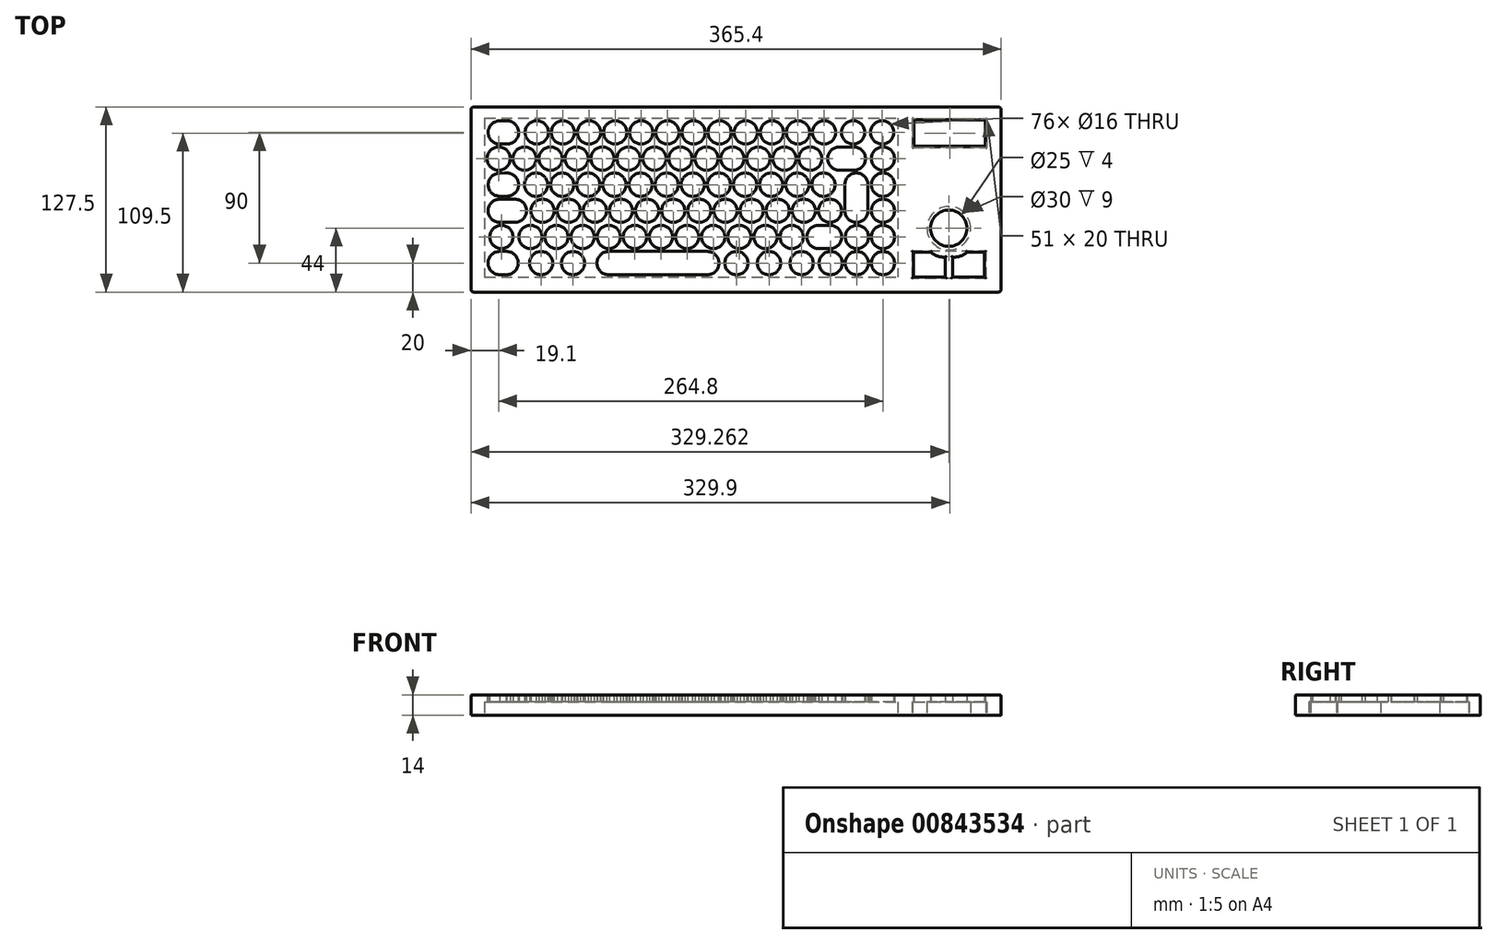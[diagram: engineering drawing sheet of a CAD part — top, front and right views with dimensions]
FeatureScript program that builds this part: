
annotation { "Feature Type Name" : "Feature", "Feature Type Description" : "" }
export const myFeature = defineFeature(function(context is Context, id is Id, definition is map)
    precondition{}
    {
        {
            var Q0;
            Q0=qCreatedBy(makeId("Top.planeOp"),FACE);
            var sketch = newSketch(context, id + "F0", { "sketchPlane" : qUnion([Q0])});
            skCircle(sketch, "E0", {"center": v(41.9, -15.35) * mm, "radius": 8 * mm});
            skLineSegment(sketch, "E1.direction1", {"start": v(41.9, -15.35) * mm, "end": v(59.9, -15.35) * mm, "construction": true});
            skCircle(sketch, "E2", {"center": v(279.9, -15.35) * mm, "radius": 8 * mm});
            skLineSegment(sketch, "E3.left", {"start": v(31.5, -15.34) * mm, "end": v(31.5, -15.34) * mm});
            skLineSegment(sketch, "E3.right", {"start": v(8.4, -15.35) * mm, "end": v(8.4, -15.35) * mm});
            skPoint(sketch, "E3.middle", {"position": v(19.95, -15.35) * mm});
            skPoint(sketch, "E4.visualSharp", {"position": v(8.4, -8.85) * mm});
            skPoint(sketch, "E5.visualSharp", {"position": v(8.4, -21.85) * mm});
            skPoint(sketch, "E6.visualSharp", {"position": v(31.5, -21.84) * mm});
            skPoint(sketch, "E7.visualSharp", {"position": v(31.5, -8.84) * mm});
            skCircle(sketch, "E8", {"center": v(280.4, -33.35) * mm, "radius": 8 * mm});
            skLineSegment(sketch, "E9.left", {"start": v(268.38, -33.35) * mm, "end": v(268.38, -33.35) * mm});
            skLineSegment(sketch, "E9.right", {"start": v(242.38, -33.35) * mm, "end": v(242.38, -33.35) * mm});
            skPoint(sketch, "E9.middle", {"position": v(255.38, -33.35) * mm});
            skPoint(sketch, "E10.visualSharp", {"position": v(242.38, -26.85) * mm});
            skPoint(sketch, "E11.visualSharp", {"position": v(242.38, -39.85) * mm});
            skPoint(sketch, "E12.visualSharp", {"position": v(268.38, -39.85) * mm});
            skPoint(sketch, "E13.visualSharp", {"position": v(268.38, -26.85) * mm});
            skCircle(sketch, "E14", {"center": v(239.4, -51.35) * mm, "radius": 8 * mm});
            skCircle(sketch, "E15", {"center": v(280.4, -51.35) * mm, "radius": 8 * mm});
            skCircle(sketch, "E16.1.0.0", {"center": v(221.4, -51.35) * mm, "radius": 8 * mm});
            skCircle(sketch, "E16.2.0.0", {"center": v(203.4, -51.35) * mm, "radius": 8 * mm});
            skCircle(sketch, "E16.3.0.0", {"center": v(185.4, -51.35) * mm, "radius": 8 * mm});
            skCircle(sketch, "E16.4.0.0", {"center": v(167.4, -51.35) * mm, "radius": 8 * mm});
            skCircle(sketch, "E16.5.0.0", {"center": v(149.4, -51.35) * mm, "radius": 8 * mm});
            skCircle(sketch, "E16.6.0.0", {"center": v(131.4, -51.35) * mm, "radius": 8 * mm});
            skCircle(sketch, "E16.7.0.0", {"center": v(113.4, -51.35) * mm, "radius": 8 * mm});
            skCircle(sketch, "E16.8.0.0", {"center": v(95.4, -51.35) * mm, "radius": 8 * mm});
            skCircle(sketch, "E16.9.0.0", {"center": v(77.4, -51.35) * mm, "radius": 8 * mm});
            skCircle(sketch, "E16.10.0.0", {"center": v(59.4, -51.35) * mm, "radius": 8 * mm});
            skCircle(sketch, "E16.11.0.0", {"center": v(41.4, -51.35) * mm, "radius": 8 * mm});
            skLineSegment(sketch, "E16.direction1", {"start": v(239.4, -51.35) * mm, "end": v(221.4, -51.35) * mm, "construction": true});
            skPoint(sketch, "E17.middle", {"position": v(19.12, -51.3) * mm});
            skCircle(sketch, "E18", {"center": v(280.4, -69.35) * mm, "radius": 8 * mm});
            skCircle(sketch, "E19", {"center": v(217.5, -87.35) * mm, "radius": 8 * mm});
            skCircle(sketch, "E20", {"center": v(262.5, -87.35) * mm, "radius": 8 * mm});
            skCircle(sketch, "E21", {"center": v(280.4, -87.35) * mm, "radius": 8 * mm});
            skLineSegment(sketch, "E22.direction1", {"start": v(217.5, -87.35) * mm, "end": v(199.5, -87.35) * mm, "construction": true});
            skPoint(sketch, "E23.middle", {"position": v(240, -87.35) * mm});
            skCircle(sketch, "E24.0.1.0", {"center": v(199.5, -87.35) * mm, "radius": 8 * mm});
            skCircle(sketch, "E24.0.2.0", {"center": v(181.5, -87.35) * mm, "radius": 8 * mm});
            skCircle(sketch, "E24.0.3.0", {"center": v(163.5, -87.35) * mm, "radius": 8 * mm});
            skCircle(sketch, "E24.0.4.0", {"center": v(145.5, -87.35) * mm, "radius": 8 * mm});
            skCircle(sketch, "E24.0.5.0", {"center": v(127.5, -87.35) * mm, "radius": 8 * mm});
            skCircle(sketch, "E24.0.6.0", {"center": v(109.5, -87.35) * mm, "radius": 8 * mm});
            skCircle(sketch, "E24.0.7.0", {"center": v(91.5, -87.35) * mm, "radius": 8 * mm});
            skCircle(sketch, "E24.0.8.0", {"center": v(73.5, -87.35) * mm, "radius": 8 * mm});
            skCircle(sketch, "E24.0.9.0", {"center": v(55.5, -87.35) * mm, "radius": 8 * mm});
            skCircle(sketch, "E24.0.10.0", {"center": v(37.5, -87.35) * mm, "radius": 8 * mm});
            skCircle(sketch, "E25", {"center": v(44.9, -105.35) * mm, "radius": 8 * mm});
            skCircle(sketch, "E26", {"center": v(66.9, -105.35) * mm, "radius": 8 * mm});
            skCircle(sketch, "E27", {"center": v(179.4, -105.35) * mm, "radius": 8 * mm});
            skCircle(sketch, "E28", {"center": v(201.9, -105.35) * mm, "radius": 8 * mm});
            skCircle(sketch, "E29", {"center": v(224.4, -105.35) * mm, "radius": 8 * mm});
            skCircle(sketch, "E30", {"center": v(244.4, -105.35) * mm, "radius": 8 * mm});
            skCircle(sketch, "E31", {"center": v(262.4, -105.35) * mm, "radius": 8 * mm});
            skCircle(sketch, "E32", {"center": v(280.4, -105.35) * mm, "radius": 8 * mm});
            skLineSegment(sketch, "E33.left", {"start": v(167.4, -105.35) * mm, "end": v(167.4, -105.35) * mm});
            skLineSegment(sketch, "E33.right", {"start": v(83.4, -105.35) * mm, "end": v(83.4, -105.35) * mm});
            skPoint(sketch, "E33.middle", {"position": v(125.4, -105.35) * mm});
            skPoint(sketch, "E34.visualSharp", {"position": v(229.5, -80.85) * mm});
            skPoint(sketch, "E35.visualSharp", {"position": v(250.5, -80.85) * mm});
            skPoint(sketch, "E36.visualSharp", {"position": v(250.5, -93.85) * mm});
            skPoint(sketch, "E37.visualSharp", {"position": v(229.5, -93.85) * mm});
            skPoint(sketch, "E38.visualSharp", {"position": v(167.4, -98.85) * mm});
            skPoint(sketch, "E39.visualSharp", {"position": v(167.4, -111.85) * mm});
            skPoint(sketch, "E40.visualSharp", {"position": v(83.4, -111.85) * mm});
            skPoint(sketch, "E41.visualSharp", {"position": v(83.4, -98.85) * mm});
            skLineSegment(sketch, "E42.bottom", {"start": v(301.9, -6.85) * mm, "end": v(350.9, -6.85) * mm});
            skLineSegment(sketch, "E42.top", {"start": v(301.9, -24.85) * mm, "end": v(350.9, -24.85) * mm});
            skLineSegment(sketch, "E42.left", {"start": v(301.9, -6.85) * mm, "end": v(301.9, -24.85) * mm});
            skLineSegment(sketch, "E42.right", {"start": v(350.9, -6.85) * mm, "end": v(350.9, -24.85) * mm});
            skCircle(sketch, "E43.0.1.0", {"center": v(59.9, -15.35) * mm, "radius": 8 * mm});
            skCircle(sketch, "E43.0.2.0", {"center": v(77.9, -15.35) * mm, "radius": 8 * mm});
            skCircle(sketch, "E43.0.3.0", {"center": v(95.9, -15.35) * mm, "radius": 8 * mm});
            skCircle(sketch, "E43.0.4.0", {"center": v(113.9, -15.35) * mm, "radius": 8 * mm});
            skCircle(sketch, "E43.0.5.0", {"center": v(131.9, -15.35) * mm, "radius": 8 * mm});
            skCircle(sketch, "E43.0.6.0", {"center": v(149.9, -15.35) * mm, "radius": 8 * mm});
            skCircle(sketch, "E43.0.7.0", {"center": v(167.9, -15.35) * mm, "radius": 8 * mm});
            skCircle(sketch, "E43.0.8.0", {"center": v(185.9, -15.35) * mm, "radius": 8 * mm});
            skCircle(sketch, "E43.0.9.0", {"center": v(203.9, -15.35) * mm, "radius": 8 * mm});
            skCircle(sketch, "E43.0.10.0", {"center": v(221.9, -15.35) * mm, "radius": 8 * mm});
            skCircle(sketch, "E43.0.11.0", {"center": v(239.9, -15.35) * mm, "radius": 8 * mm});
            skCircle(sketch, "E44", {"center": v(259.9, -15.35) * mm, "radius": 8 * mm});
            skCircle(sketch, "E45", {"center": v(17.5, -87.35) * mm, "radius": 8 * mm});
            skCircle(sketch, "E46", {"center": v(243.9, -69.35) * mm, "radius": 8 * mm});
            skLineSegment(sketch, "E47.direction1", {"start": v(243.9, -69.35) * mm, "end": v(225.9, -69.35) * mm, "construction": true});
            skLineSegment(sketch, "E48", {"start": v(361.9, 0.15) * mm, "end": v(361.9, -123.35) * mm});
            skLineSegment(sketch, "E49", {"start": v(301.4, -114.85) * mm, "end": v(301.4, -97.85) * mm});
            skLineSegment(sketch, "E50", {"start": v(301.4, -97.85) * mm, "end": v(313.4, -97.85) * mm});
            skLineSegment(sketch, "E51", {"start": v(301.4, -114.85) * mm, "end": v(323.4, -114.85) * mm});
            skLineSegment(sketch, "E52", {"start": v(323.4, -114.85) * mm, "end": v(323.4, -101.35) * mm});
            skLineSegment(sketch, "E53", {"start": v(328.4, -101.35) * mm, "end": v(328.4, -114.85) * mm});
            skLineSegment(sketch, "E54", {"start": v(328.4, -114.85) * mm, "end": v(350.4, -114.85) * mm});
            skLineSegment(sketch, "E55", {"start": v(350.4, -114.85) * mm, "end": v(350.4, -97.85) * mm});
            skLineSegment(sketch, "E56", {"start": v(350.4, -97.85) * mm, "end": v(338.4, -97.85) * mm});
            skArc(sketch, "E57", {"start": v(313.4, -97.85) * mm, "mid": v(318.08, -100.51) * mm, "end": v(323.4, -101.35) * mm});
            skArc(sketch, "E58", {"start": v(328.4, -101.35) * mm, "mid": v(333.72, -100.51) * mm, "end": v(338.4, -97.85) * mm});
            skCircle(sketch, "E59", {"center": v(325.76, -81.35) * mm, "radius": 12.5 * mm});
            skCircle(sketch, "E60", {"center": v(230.4, -33.35) * mm, "radius": 8 * mm});
            skCircle(sketch, "E61.1.0.0", {"center": v(212.5, -33.35) * mm, "radius": 8 * mm});
            skCircle(sketch, "E61.2.0.0", {"center": v(194.6, -33.35) * mm, "radius": 8 * mm});
            skCircle(sketch, "E61.3.0.0", {"center": v(176.7, -33.35) * mm, "radius": 8 * mm});
            skCircle(sketch, "E61.4.0.0", {"center": v(158.8, -33.35) * mm, "radius": 8 * mm});
            skCircle(sketch, "E61.5.0.0", {"center": v(140.9, -33.35) * mm, "radius": 8 * mm});
            skCircle(sketch, "E61.6.0.0", {"center": v(123, -33.35) * mm, "radius": 8 * mm});
            skCircle(sketch, "E61.7.0.0", {"center": v(105.1, -33.35) * mm, "radius": 8 * mm});
            skCircle(sketch, "E61.8.0.0", {"center": v(87.2, -33.35) * mm, "radius": 8 * mm});
            skCircle(sketch, "E61.9.0.0", {"center": v(69.3, -33.35) * mm, "radius": 8 * mm});
            skCircle(sketch, "E61.10.0.0", {"center": v(51.4, -33.35) * mm, "radius": 8 * mm});
            skCircle(sketch, "E61.11.0.0", {"center": v(33.5, -33.35) * mm, "radius": 8 * mm});
            skCircle(sketch, "E61.12.0.0", {"center": v(15.6, -33.35) * mm, "radius": 8 * mm});
            skLineSegment(sketch, "E61.direction1", {"start": v(230.4, -33.35) * mm, "end": v(212.5, -33.35) * mm, "construction": true});
            skCircle(sketch, "E62.0.1.0", {"center": v(225.9, -69.35) * mm, "radius": 8 * mm});
            skCircle(sketch, "E62.0.2.0", {"center": v(207.9, -69.35) * mm, "radius": 8 * mm});
            skCircle(sketch, "E62.0.3.0", {"center": v(189.9, -69.35) * mm, "radius": 8 * mm});
            skCircle(sketch, "E62.0.4.0", {"center": v(171.9, -69.35) * mm, "radius": 8 * mm});
            skCircle(sketch, "E62.0.5.0", {"center": v(153.9, -69.35) * mm, "radius": 8 * mm});
            skCircle(sketch, "E62.0.6.0", {"center": v(135.9, -69.35) * mm, "radius": 8 * mm});
            skCircle(sketch, "E62.0.7.0", {"center": v(117.9, -69.35) * mm, "radius": 8 * mm});
            skCircle(sketch, "E62.0.8.0", {"center": v(99.9, -69.35) * mm, "radius": 8 * mm});
            skCircle(sketch, "E62.0.9.0", {"center": v(81.9, -69.35) * mm, "radius": 8 * mm});
            skCircle(sketch, "E62.0.10.0", {"center": v(63.9, -69.35) * mm, "radius": 8 * mm});
            skCircle(sketch, "E62.0.11.0", {"center": v(45.9, -69.35) * mm, "radius": 8 * mm});
            skPoint(sketch, "E63.endSnap0", {"position": v(280.4, -96.35) * mm});
            skArc(sketch, "E64", {"start": v(91.4, -97.35) * mm, "mid": v(83.4, -105.35) * mm, "end": v(91.4, -113.35) * mm});
            skArc(sketch, "E65", {"start": v(159.4, -113.35) * mm, "mid": v(167.4, -105.35) * mm, "end": v(159.4, -97.35) * mm});
            skLineSegment(sketch, "E66", {"start": v(91.4, -97.35) * mm, "end": v(159.4, -97.35) * mm});
            skLineSegment(sketch, "E67", {"start": v(91.4, -113.35) * mm, "end": v(159.4, -113.35) * mm});
            skArc(sketch, "E68", {"start": v(250.38, -25.35) * mm, "mid": v(242.38, -33.35) * mm, "end": v(250.38, -41.35) * mm});
            skArc(sketch, "E69", {"start": v(260.38, -41.35) * mm, "mid": v(268.38, -33.35) * mm, "end": v(260.38, -25.35) * mm});
            skLineSegment(sketch, "E70", {"start": v(250.38, -25.35) * mm, "end": v(260.38, -25.35) * mm});
            skLineSegment(sketch, "E71", {"start": v(260.38, -41.35) * mm, "end": v(250.38, -41.35) * mm});
            skArc(sketch, "E72", {"start": v(254.15, -69.35) * mm, "mid": v(262.15, -77.35) * mm, "end": v(270.15, -69.35) * mm});
            skArc(sketch, "E73", {"start": v(270.15, -51.35) * mm, "mid": v(262.15, -43.35) * mm, "end": v(254.15, -51.35) * mm});
            skLineSegment(sketch, "E74", {"start": v(254.15, -51.35) * mm, "end": v(254.15, -69.35) * mm});
            skLineSegment(sketch, "E75", {"start": v(270.15, -69.35) * mm, "end": v(270.15, -51.35) * mm});
            skPoint(sketch, "E76.start.orphan", {"position": v(272.4, -69.35) * mm});
            skArc(sketch, "E77", {"start": v(244, -95.35) * mm, "mid": v(252, -87.35) * mm, "end": v(244, -79.35) * mm});
            skLineSegment(sketch, "E78", {"start": v(236, -79.35) * mm, "end": v(244, -79.35) * mm});
            skLineSegment(sketch, "E79", {"start": v(244, -95.35) * mm, "end": v(236, -95.35) * mm});
            skPoint(sketch, "E36.filletArc.start.orphan", {"position": v(244, -93.85) * mm});
            skPoint(sketch, "E80.orphan", {"position": v(244, -80.85) * mm});
            skArc(sketch, "E81.trimOffspring", {"start": v(236, -79.35) * mm, "mid": v(228, -87.35) * mm, "end": v(236, -95.35) * mm});
            skPoint(sketch, "E34.filletArc.start.orphan", {"position": v(236, -80.85) * mm});
            skPoint(sketch, "E37.filletArc.end.orphan", {"position": v(236, -93.85) * mm});
            skArc(sketch, "E82", {"start": v(16.4, -7.37) * mm, "mid": v(8.4, -15.38) * mm, "end": v(16.43, -23.37) * mm});
            skArc(sketch, "E83", {"start": v(21.4, -23.35) * mm, "mid": v(29.4, -15.06) * mm, "end": v(20.83, -7.37) * mm});
            skLineSegment(sketch, "E84", {"start": v(16.43, -23.37) * mm, "end": v(21.4, -23.35) * mm});
            skLineSegment(sketch, "E85", {"start": v(16.4, -7.37) * mm, "end": v(21.4, -7.37) * mm});
            skLineSegment(sketch, "E86", {"start": v(8.33, -51.32) * mm, "end": v(8.4, -51.32) * mm});
            skArc(sketch, "E87", {"start": v(16.33, -43.44) * mm, "mid": v(8.4, -51.37) * mm, "end": v(16.33, -59.3) * mm});
            skArc(sketch, "E88", {"start": v(21.24, -59.3) * mm, "mid": v(29.33, -51.1) * mm, "end": v(20.87, -43.3) * mm});
            skLineSegment(sketch, "E89", {"start": v(16.33, -43.44) * mm, "end": v(21.33, -43.3) * mm});
            skLineSegment(sketch, "E90", {"start": v(21.42, -59.3) * mm, "end": v(16.33, -59.3) * mm});
            skArc(sketch, "E91", {"start": v(16.34, -61.35) * mm, "mid": v(8.34, -69.35) * mm, "end": v(16.34, -77.35) * mm});
            skArc(sketch, "E92", {"start": v(26.84, -77.35) * mm, "mid": v(34.84, -69.35) * mm, "end": v(26.84, -61.35) * mm});
            skLineSegment(sketch, "E93", {"start": v(16.34, -61.35) * mm, "end": v(26.84, -61.35) * mm});
            skLineSegment(sketch, "E94", {"start": v(16.34, -77.35) * mm, "end": v(26.84, -77.35) * mm});
            skArc(sketch, "E95", {"start": v(16.3, -97.33) * mm, "mid": v(8.3, -105.33) * mm, "end": v(16.3, -113.33) * mm});
            skArc(sketch, "E96", {"start": v(21.11, -113.33) * mm, "mid": v(29.11, -105.33) * mm, "end": v(21.11, -97.33) * mm});
            skLineSegment(sketch, "E97", {"start": v(16.3, -97.33) * mm, "end": v(21.11, -97.33) * mm});
            skLineSegment(sketch, "E98", {"start": v(21.11, -113.33) * mm, "end": v(16.3, -113.33) * mm});
            skLineSegment(sketch, "E99.bottom", {"start": v(5.98, -5.47) * mm, "end": v(290.54, -5.47) * mm});
            skLineSegment(sketch, "E99.top", {"start": v(5.98, -114.85) * mm, "end": v(290.54, -114.85) * mm});
            skLineSegment(sketch, "E99.left", {"start": v(5.98, -5.47) * mm, "end": v(5.98, -114.85) * mm});
            skLineSegment(sketch, "E99.right", {"start": v(290.54, -5.47) * mm, "end": v(290.54, -114.85) * mm});
            skLineSegment(sketch, "E100", {"start": v(353.9, -117.35) * mm, "end": v(353.9, -3.85) * mm});
            skLineSegment(sketch, "E101", {"start": v(353.9, -117.35) * mm, "end": v(4.5, -117.35) * mm});
            skLineSegment(sketch, "E102", {"start": v(4.5, -117.35) * mm, "end": v(4.5, -3.85) * mm});
            skLineSegment(sketch, "E103", {"start": v(4.5, -3.85) * mm, "end": v(353.9, -3.85) * mm});
            skCircle(sketch, "E104", {"center": v(325.76, -81.35) * mm, "radius": 15 * mm});
            skLineSegment(sketch, "E105.top", {"start": v(301.4, -115.85) * mm, "end": v(300.4, -115.85) * mm});
            skLineSegment(sketch, "E105.right", {"start": v(300.4, -114.85) * mm, "end": v(300.4, -115.85) * mm});
            skLineSegment(sketch, "E106.top", {"start": v(350.4, -96.85) * mm, "end": v(351.4, -96.85) * mm});
            skLineSegment(sketch, "E106.right", {"start": v(351.4, -97.85) * mm, "end": v(351.4, -96.85) * mm});
            skLineSegment(sketch, "E107.bottom", {"start": v(351.4, -96.85) * mm, "end": v(300.4, -96.85) * mm});
            skLineSegment(sketch, "E107.top", {"start": v(351.4, -115.85) * mm, "end": v(300.4, -115.85) * mm});
            skLineSegment(sketch, "E107.left", {"start": v(351.4, -96.85) * mm, "end": v(351.4, -115.85) * mm});
            skLineSegment(sketch, "E107.right", {"start": v(300.4, -96.85) * mm, "end": v(300.4, -115.85) * mm});
            skLineSegment(sketch, "E108.top", {"start": v(350.9, -25.85) * mm, "end": v(351.9, -25.85) * mm});
            skLineSegment(sketch, "E108.right", {"start": v(351.9, -24.85) * mm, "end": v(351.9, -25.85) * mm});
            skLineSegment(sketch, "E109.top", {"start": v(301.9, -5.85) * mm, "end": v(300.9, -5.85) * mm});
            skLineSegment(sketch, "E109.right", {"start": v(300.9, -6.85) * mm, "end": v(300.9, -5.85) * mm});
            skLineSegment(sketch, "E110.bottom", {"start": v(300.9, -5.85) * mm, "end": v(351.9, -5.85) * mm});
            skLineSegment(sketch, "E110.top", {"start": v(300.9, -25.85) * mm, "end": v(351.9, -25.85) * mm});
            skLineSegment(sketch, "E110.left", {"start": v(300.9, -5.85) * mm, "end": v(300.9, -25.85) * mm});
            skLineSegment(sketch, "E110.right", {"start": v(351.9, -5.85) * mm, "end": v(351.9, -25.85) * mm});
            skLineSegment(sketch, "E111", {"start": v(-1.5, 2.15) * mm, "end": v(359.9, 2.15) * mm});
            skLineSegment(sketch, "E112", {"start": v(-1.5, -125.35) * mm, "end": v(359.9, -125.35) * mm});
            skLineSegment(sketch, "E113", {"start": v(-3.5, -123.35) * mm, "end": v(-3.5, 0.15) * mm});
            skPoint(sketch, "E114.visualSharp", {"position": v(-3.5, 2.15) * mm});
            skArc(sketch, "E114.filletArc", {"start": v(-1.5, 2.15) * mm, "mid": v(-2.91, 1.56) * mm, "end": v(-3.5, 0.15) * mm});
            skPoint(sketch, "E115.visualSharp", {"position": v(-3.5, -125.35) * mm});
            skArc(sketch, "E115.filletArc", {"start": v(-3.5, -123.35) * mm, "mid": v(-2.91, -124.76) * mm, "end": v(-1.5, -125.35) * mm});
            skPoint(sketch, "E116.visualSharp", {"position": v(361.9, -125.35) * mm});
            skArc(sketch, "E116.filletArc", {"start": v(359.9, -125.35) * mm, "mid": v(361.31, -124.76) * mm, "end": v(361.9, -123.35) * mm});
            skPoint(sketch, "E117.visualSharp", {"position": v(361.9, 2.15) * mm});
            skArc(sketch, "E117.filletArc", {"start": v(361.9, 0.15) * mm, "mid": v(361.31, 1.56) * mm, "end": v(359.9, 2.15) * mm});
            skSolve(sketch);
        }
        {
            var Q0;
            Q0=makeQuery(id+"F0.imprint","IMPRINT",FACE,{"disambiguationData":[TD([[makeQuery(id+"F0.imprint","IMPRINT",EDGE,{"derivedFrom":sQuery(id+"F0.wireOp",EDGE,"T8WCm78W-SvFY-fUnR-yLuJ-OhTCZNTdzIay")}),1.0]])]});
            var Q1;
            {var subQ17=sQuery(id+"F0.wireOp",EDGE,"mFOY19iY-rQF4-OdMh-8pD4-EtOYxX6kkBAH");Q1=makeQuery(id+"F0.imprint","IMPRINT",FACE,{"disambiguationData":[TD([[makeQuery(id+"F0.imprint","IMPRINT",EDGE,{"derivedFrom":subQ17}),1.0]])]});}
            var Q2;
            {var subQ4=sQuery(id+"F0.wireOp",EDGE,"O5om7XPq-pfzq-tTJn-29gd-RDgdcxbKojAD");Q2=makeQuery(id+"F0.imprint","IMPRINT",FACE,{"disambiguationData":[TD([[makeQuery(id+"F0.imprint","IMPRINT",EDGE,{"derivedFrom":subQ4}),-1.0]])]});}
            var Q3;
            {var subQ9=sQuery(id+"F0.wireOp",EDGE,"mFOY19iY-rQF4-OdMh-8pD4-EtOYxX6kkBAH");Q3=makeQuery(id+"F0.imprint","IMPRINT",FACE,{"disambiguationData":[TD([[makeQuery(id+"F0.imprint","IMPRINT",EDGE,{"derivedFrom":subQ9}),-1.0]])]});}
            var Q4;
            {var subQ1=sQuery(id+"F0.wireOp",EDGE,"E42.top");Q4=makeQuery(id+"F0.imprint","IMPRINT",FACE,{"disambiguationData":[TD([[makeQuery(id+"F0.imprint","IMPRINT",EDGE,{"derivedFrom":subQ1}),-1.0]])]});}
            var Q5;
            {var subQ0=sQuery(id+"F0.wireOp",EDGE,"IOk0f0ik-m6Pr-axO5-sAgc-cp6PbQEXwRWr");var subQ2=sQuery(id+"F0.wireOp",EDGE,"LzY9nmAe-SVTQ-qMCv-zxcc-P1EQXe39lv1v");var subQ3=makeQuery(id+"F0.imprint","INTERSECT",VERTEX,{"derivedFrom":[subQ2,subQ0]});Q5=makeQuery(id+"F0.imprint","IMPRINT",FACE,{"disambiguationData":[TD([[makeQuery(id+"F0.imprint","IMPRINT",EDGE,{"disambiguationData":[TD([[subQ3,-1.0]])],"derivedFrom":subQ2}),-1.0]])]});}
            var Q6;
            {var subQ7=sQuery(id+"F0.wireOp",EDGE,"IOk0f0ik-m6Pr-axO5-sAgc-cp6PbQEXwRWr");var subQ9=sQuery(id+"F0.wireOp",EDGE,"LzY9nmAe-SVTQ-qMCv-zxcc-P1EQXe39lv1v");var subQ10=makeQuery(id+"F0.imprint","INTERSECT",VERTEX,{"derivedFrom":[subQ9,subQ7]});Q6=makeQuery(id+"F0.imprint","IMPRINT",FACE,{"disambiguationData":[TD([[makeQuery(id+"F0.imprint","IMPRINT",EDGE,{"disambiguationData":[TD([[subQ10,-1.0]])],"derivedFrom":subQ9}),1.0]])]});}
            var Q7;
            {var subQ5=sQuery(id+"F0.wireOp",EDGE,"7YK5K3SY-gkoG-W7Ew-9AiD-mYzw7hBbQorf");Q7=makeQuery(id+"F0.imprint","IMPRINT",FACE,{"disambiguationData":[TD([[makeQuery(id+"F0.imprint","IMPRINT",EDGE,{"derivedFrom":subQ5}),1.0]])]});}
            var Q8;
            {var subQ5=sQuery(id+"F0.wireOp",EDGE,"LzY9nmAe-SVTQ-qMCv-zxcc-P1EQXe39lv1v");var subQ6=makeQuery(id+"F0.imprint","INTERSECT",VERTEX,{"derivedFrom":[subQ5,sQuery(id+"F0.wireOp",EDGE,"PkYXxiHH-amAg-5pAi-YDFA-uypcR8lKY2Dw")]});Q8=makeQuery(id+"F0.imprint","IMPRINT",FACE,{"disambiguationData":[TD([[makeQuery(id+"F0.imprint","IMPRINT",EDGE,{"disambiguationData":[TD([[subQ6,1.0]])],"derivedFrom":subQ5}),1.0]])]});}
            var Q9;
            {var subQ10=sQuery(id+"F0.wireOp",EDGE,"PkYXxiHH-amAg-5pAi-YDFA-uypcR8lKY2Dw");Q9=makeQuery(id+"F0.imprint","IMPRINT",FACE,{"disambiguationData":[TD([[makeQuery(id+"F0.imprint","IMPRINT",EDGE,{"derivedFrom":subQ10}),-1.0]])]});}
            var Q10;
            {var subQ0=sQuery(id+"F0.wireOp",EDGE,"55b4ee8d-2d37-449f-8af8-b3f63763dadd");Q10=makeQuery(id+"F0.imprint","IMPRINT",FACE,{"disambiguationData":[TD([[makeQuery(id+"F0.imprint","IMPRINT",EDGE,{"derivedFrom":subQ0}),1.0]])]});}
            var Q11;
            {var subQ0=sQuery(id+"F0.wireOp",EDGE,"PkYXxiHH-amAg-5pAi-YDFA-uypcR8lKY2Dw");Q11=makeQuery(id+"F0.imprint","IMPRINT",FACE,{"disambiguationData":[TD([[makeQuery(id+"F0.imprint","IMPRINT",EDGE,{"derivedFrom":subQ0}),1.0]])]});}
            var Q12;
            {var subQ0=sQuery(id+"F0.wireOp",EDGE,"2K1XfT52-QnSG-LakS-bHGF-tO5ZBf05Ys4U");Q12=makeQuery(id+"F0.imprint","IMPRINT",FACE,{"disambiguationData":[TD([[makeQuery(id+"F0.imprint","IMPRINT",EDGE,{"derivedFrom":subQ0}),-1.0]])]});}
            var Q13;
            {var subQ7=sQuery(id+"F0.wireOp",EDGE,"DqwtAA8F-Toou-zgQl-Itcw-aFaVFGqcLjSK");Q13=makeQuery(id+"F0.imprint","IMPRINT",FACE,{"disambiguationData":[TD([[makeQuery(id+"F0.imprint","IMPRINT",EDGE,{"derivedFrom":subQ7}),1.0]])]});}
            var Q14;
            {var subQ0=sQuery(id+"F0.wireOp",EDGE,"eA3PdnsC-yLSK-XZ79-eB5l-IwCOXOp0draJ");var subQ1=sQuery(id+"F0.wireOp",EDGE,"T8WCm78W-SvFY-fUnR-yLuJ-OhTCZNTdzIay");var subQ2=makeQuery(id+"F0.imprint","INTERSECT",VERTEX,{"derivedFrom":[subQ1,subQ0]});Q14=makeQuery(id+"F0.imprint","IMPRINT",FACE,{"disambiguationData":[TD([[makeQuery(id+"F0.imprint","IMPRINT",EDGE,{"disambiguationData":[TD([[subQ2,1.0]])],"derivedFrom":subQ1}),-1.0]])]});}
            var Q15;
            {var subQ13=sQuery(id+"F0.wireOp",EDGE,"E50");Q15=makeQuery(id+"F0.imprint","IMPRINT",FACE,{"disambiguationData":[TD([[makeQuery(id+"F0.imprint","IMPRINT",EDGE,{"derivedFrom":subQ13}),1.0]])]});}
            var Q16;
            {var subQ0=sQuery(id+"F0.wireOp",EDGE,"E63");var subQ1=sQuery(id+"F0.wireOp",EDGE,"E32");var subQ2=makeQuery(id+"F0.imprint","INTERSECT",VERTEX,{"derivedFrom":[subQ1,subQ0]});Q16=makeQuery(id+"F0.imprint","IMPRINT",FACE,{"disambiguationData":[TD([[makeQuery(id+"F0.imprint","IMPRINT",EDGE,{"disambiguationData":[TD([[subQ2,1.0]])],"derivedFrom":subQ1}),-1.0]])]});}
            var Q17;
            {var subQ0=sQuery(id+"F0.wireOp",EDGE,"5ppePVbm-UdDY-gURY-IQdl-TF3jMLGd08k3");Q17=makeQuery(id+"F0.imprint","IMPRINT",FACE,{"disambiguationData":[TD([[makeQuery(id+"F0.imprint","IMPRINT",EDGE,{"derivedFrom":subQ0}),-1.0]])]});}
            var Q18;
            {var subQ3=sQuery(id+"F0.wireOp",EDGE,"0MQXd9Ix-655c-Acjm-5W3v-4LVtmzEtWtHO");var subQ7=sQuery(id+"F0.wireOp",EDGE,"T8WCm78W-SvFY-fUnR-yLuJ-OhTCZNTdzIay");var subQ8=makeQuery(id+"F0.imprint","INTERSECT",VERTEX,{"derivedFrom":[subQ7,subQ3]});Q18=makeQuery(id+"F0.imprint","IMPRINT",FACE,{"disambiguationData":[TD([[makeQuery(id+"F0.imprint","IMPRINT",EDGE,{"disambiguationData":[TD([[subQ8,-1.0]])],"derivedFrom":subQ7}),-1.0]])]});}
            var Q19;
            {var subQ1=sQuery(id+"F0.wireOp",EDGE,"E54");Q19=makeQuery(id+"F0.imprint","IMPRINT",FACE,{"disambiguationData":[TD([[makeQuery(id+"F0.imprint","IMPRINT",EDGE,{"derivedFrom":subQ1}),-1.0]])]});}
            var Q20;
            Q20=makeQuery(id+"F0.imprint","IMPRINT",FACE,{"disambiguationData":[TD([[makeQuery(id+"F0.imprint","IMPRINT",EDGE,{"derivedFrom":sQuery(id+"F0.wireOp",EDGE,"0rU5M5Sb-Wbeh-3Pnk-K0j0-Pg7QML7mU2cz.bottom")}),1.0]])]});
            var Q21;
            Q21=makeQuery(id+"F0.imprint","IMPRINT",FACE,{"disambiguationData":[TD([[makeQuery(id+"F0.imprint","IMPRINT",EDGE,{"derivedFrom":sQuery(id+"F0.wireOp",EDGE,"E99.bottom")}),1.0]])]});
            var Q22;
            Q22=makeQuery(id+"F0.imprint","IMPRINT",FACE,{"disambiguationData":[TD([[makeQuery(id+"F0.imprint","IMPRINT",EDGE,{"derivedFrom":sQuery(id+"F0.wireOp",EDGE,"E59")}),-1.0]])]});
            var Q23;
            Q23=makeQuery(id+"F0.imprint","IMPRINT",FACE,{"disambiguationData":[TD([[makeQuery(id+"F0.imprint","IMPRINT",EDGE,{"derivedFrom":sQuery(id+"F0.wireOp",EDGE,"E48")}),-1.0]])]});
            extrude(context, id + "F1", {"entities" : qUnion([Q0, Q1, Q2, Q3, Q4, Q5, Q6, Q7, Q8, Q9, Q10, Q11, Q12, Q13, Q14, Q15, Q16, Q17, Q18, Q19, Q20, Q21, Q22, Q23]), "depth" : 14 * mm, "offsetDistance" : 25 * mm});
        }
        {
            var Q0;
            Q0=makeQuery(id+"F1.opExtrude","CAP_FACE",FACE,{"disambiguationData":[OSD([sQuery(id+"F0.wireOp",EDGE,"E0"),sQuery(id+"F0.wireOp",EDGE,"E2"),sQuery(id+"F0.wireOp",EDGE,"E3.bottom"),sQuery(id+"F0.wireOp",EDGE,"E3.top"),sQuery(id+"F0.wireOp",EDGE,"E4.filletArc"),sQuery(id+"F0.wireOp",EDGE,"E5.filletArc"),sQuery(id+"F0.wireOp",EDGE,"E6.filletArc"),sQuery(id+"F0.wireOp",EDGE,"E7.filletArc"),sQuery(id+"F0.wireOp",EDGE,"E8"),sQuery(id+"F0.wireOp",EDGE,"E14"),sQuery(id+"F0.wireOp",EDGE,"E15"),sQuery(id+"F0.wireOp",EDGE,"E16.1.0.0"),sQuery(id+"F0.wireOp",EDGE,"E16.2.0.0"),sQuery(id+"F0.wireOp",EDGE,"E16.3.0.0"),sQuery(id+"F0.wireOp",EDGE,"E16.4.0.0"),sQuery(id+"F0.wireOp",EDGE,"E16.5.0.0"),sQuery(id+"F0.wireOp",EDGE,"E16.6.0.0"),sQuery(id+"F0.wireOp",EDGE,"E16.7.0.0"),sQuery(id+"F0.wireOp",EDGE,"E16.8.0.0"),sQuery(id+"F0.wireOp",EDGE,"E16.9.0.0"),sQuery(id+"F0.wireOp",EDGE,"E16.10.0.0"),sQuery(id+"F0.wireOp",EDGE,"E16.11.0.0"),sQuery(id+"F0.wireOp",EDGE,"E18"),sQuery(id+"F0.wireOp",EDGE,"E19"),sQuery(id+"F0.wireOp",EDGE,"E20"),sQuery(id+"F0.wireOp",EDGE,"E21"),sQuery(id+"F0.wireOp",EDGE,"E23.bottom"),sQuery(id+"F0.wireOp",EDGE,"E23.top"),sQuery(id+"F0.wireOp",EDGE,"E24.0.1.0"),sQuery(id+"F0.wireOp",EDGE,"E24.0.2.0"),sQuery(id+"F0.wireOp",EDGE,"E24.0.3.0"),sQuery(id+"F0.wireOp",EDGE,"E24.0.4.0"),sQuery(id+"F0.wireOp",EDGE,"E24.0.5.0"),sQuery(id+"F0.wireOp",EDGE,"E24.0.6.0"),sQuery(id+"F0.wireOp",EDGE,"E24.0.7.0"),sQuery(id+"F0.wireOp",EDGE,"E24.0.8.0"),sQuery(id+"F0.wireOp",EDGE,"E24.0.9.0"),sQuery(id+"F0.wireOp",EDGE,"E24.0.10.0"),sQuery(id+"F0.wireOp",EDGE,"E25"),sQuery(id+"F0.wireOp",EDGE,"E26"),sQuery(id+"F0.wireOp",EDGE,"E27"),sQuery(id+"F0.wireOp",EDGE,"E28"),sQuery(id+"F0.wireOp",EDGE,"E29"),sQuery(id+"F0.wireOp",EDGE,"E30"),sQuery(id+"F0.wireOp",EDGE,"E31"),sQuery(id+"F0.wireOp",EDGE,"E32"),sQuery(id+"F0.wireOp",EDGE,"E34.filletArc"),sQuery(id+"F0.wireOp",EDGE,"E35.filletArc"),sQuery(id+"F0.wireOp",EDGE,"E36.filletArc"),sQuery(id+"F0.wireOp",EDGE,"E37.filletArc"),sQuery(id+"F0.wireOp",EDGE,"E42.bottom"),sQuery(id+"F0.wireOp",EDGE,"E42.top"),sQuery(id+"F0.wireOp",EDGE,"E42.left"),sQuery(id+"F0.wireOp",EDGE,"E42.right"),sQuery(id+"F0.wireOp",EDGE,"0rU5M5Sb-Wbeh-3Pnk-K0j0-Pg7QML7mU2cz.bottom"),sQuery(id+"F0.wireOp",EDGE,"0rU5M5Sb-Wbeh-3Pnk-K0j0-Pg7QML7mU2cz.top"),sQuery(id+"F0.wireOp",EDGE,"0rU5M5Sb-Wbeh-3Pnk-K0j0-Pg7QML7mU2cz.right"),sQuery(id+"F0.wireOp",EDGE,"E43.0.1.0"),sQuery(id+"F0.wireOp",EDGE,"E43.0.2.0"),sQuery(id+"F0.wireOp",EDGE,"E43.0.3.0"),sQuery(id+"F0.wireOp",EDGE,"E43.0.4.0"),sQuery(id+"F0.wireOp",EDGE,"E43.0.5.0"),sQuery(id+"F0.wireOp",EDGE,"E43.0.6.0"),sQuery(id+"F0.wireOp",EDGE,"E43.0.7.0"),sQuery(id+"F0.wireOp",EDGE,"E43.0.8.0"),sQuery(id+"F0.wireOp",EDGE,"E43.0.9.0"),sQuery(id+"F0.wireOp",EDGE,"E43.0.10.0"),sQuery(id+"F0.wireOp",EDGE,"E43.0.11.0"),sQuery(id+"F0.wireOp",EDGE,"E44"),sQuery(id+"F0.wireOp",EDGE,"E45"),sQuery(id+"F0.wireOp",EDGE,"E46"),sQuery(id+"F0.wireOp",EDGE,"E48"),sQuery(id+"F0.wireOp",EDGE,"E49"),sQuery(id+"F0.wireOp",EDGE,"E50"),sQuery(id+"F0.wireOp",EDGE,"E51"),sQuery(id+"F0.wireOp",EDGE,"E52"),sQuery(id+"F0.wireOp",EDGE,"E53"),sQuery(id+"F0.wireOp",EDGE,"E54"),sQuery(id+"F0.wireOp",EDGE,"E55"),sQuery(id+"F0.wireOp",EDGE,"E56"),sQuery(id+"F0.wireOp",EDGE,"E57"),sQuery(id+"F0.wireOp",EDGE,"E58"),sQuery(id+"F0.wireOp",EDGE,"E59"),sQuery(id+"F0.wireOp",EDGE,"E60"),sQuery(id+"F0.wireOp",EDGE,"E61.1.0.0"),sQuery(id+"F0.wireOp",EDGE,"E61.2.0.0"),sQuery(id+"F0.wireOp",EDGE,"E61.3.0.0"),sQuery(id+"F0.wireOp",EDGE,"E61.4.0.0"),sQuery(id+"F0.wireOp",EDGE,"E61.5.0.0"),sQuery(id+"F0.wireOp",EDGE,"E61.6.0.0"),sQuery(id+"F0.wireOp",EDGE,"E61.7.0.0"),sQuery(id+"F0.wireOp",EDGE,"E61.8.0.0"),sQuery(id+"F0.wireOp",EDGE,"E61.9.0.0"),sQuery(id+"F0.wireOp",EDGE,"E61.10.0.0"),sQuery(id+"F0.wireOp",EDGE,"E61.11.0.0"),sQuery(id+"F0.wireOp",EDGE,"E61.12.0.0"),sQuery(id+"F0.wireOp",EDGE,"E62.0.1.0"),sQuery(id+"F0.wireOp",EDGE,"E62.0.2.0"),sQuery(id+"F0.wireOp",EDGE,"E62.0.3.0"),sQuery(id+"F0.wireOp",EDGE,"E62.0.4.0"),sQuery(id+"F0.wireOp",EDGE,"E62.0.5.0"),sQuery(id+"F0.wireOp",EDGE,"E62.0.6.0"),sQuery(id+"F0.wireOp",EDGE,"E62.0.7.0"),sQuery(id+"F0.wireOp",EDGE,"E62.0.8.0"),sQuery(id+"F0.wireOp",EDGE,"E62.0.9.0"),sQuery(id+"F0.wireOp",EDGE,"E62.0.10.0"),sQuery(id+"F0.wireOp",EDGE,"E62.0.11.0"),sQuery(id+"F0.wireOp",EDGE,"E64"),sQuery(id+"F0.wireOp",EDGE,"E65"),sQuery(id+"F0.wireOp",EDGE,"E66"),sQuery(id+"F0.wireOp",EDGE,"E67"),sQuery(id+"F0.wireOp",EDGE,"T4mSVnlP-qbPE-Wta1-vFse-OfULQgZifXzC"),sQuery(id+"F0.wireOp",EDGE,"0krP5LN1-WmEM-zpcz-fhZC-gV7xdUvbeYy7"),sQuery(id+"F0.wireOp",EDGE,"r3waRWo6-iW0L-meTu-aTAE-DQFJgrG0CUte"),sQuery(id+"F0.wireOp",EDGE,"EnCBTEJ6-Bw90-k6p9-zkUJ-4Hvkvc13zNgY"),sQuery(id+"F0.wireOp",EDGE,"6VRb7CxG-vvd0-6Ear-184h-eAD7FWq39BAb"),sQuery(id+"F0.wireOp",EDGE,"DrH2VswD-LdPR-93tt-7dVm-Op18F2VKbW0G"),sQuery(id+"F0.wireOp",EDGE,"QeyCogB7-UIcp-MVJ9-3z6C-TOtN1lgbzRFD"),sQuery(id+"F0.wireOp",EDGE,"DqwtAA8F-Toou-zgQl-Itcw-aFaVFGqcLjSK"),sQuery(id+"F0.wireOp",EDGE,"E68"),sQuery(id+"F0.wireOp",EDGE,"E69"),sQuery(id+"F0.wireOp",EDGE,"E70"),sQuery(id+"F0.wireOp",EDGE,"E71"),sQuery(id+"F0.wireOp",EDGE,"TLAxFEVW-QNiw-S5IW-MYy1-3jP50XOABxDr"),sQuery(id+"F0.wireOp",EDGE,"2c43D8hS-7ORO-aWTW-UuJG-exZux8KKtWMf"),sQuery(id+"F0.wireOp",EDGE,"nZiHykA3-aEoW-XX3b-xLcg-g9MvtjQaqwNa"),sQuery(id+"F0.wireOp",EDGE,"67tKMlyM-dZyj-MAAs-RrUI-zJsYxZ2BhLxT"),sQuery(id+"F0.wireOp",EDGE,"PAliD9Ka-i9VF-RgpA-PUxI-8RMOAZ441GKP"),sQuery(id+"F0.wireOp",EDGE,"EkLHfyVJ-3RyJ-X3Ba-GLdX-SzsZ4757wEsa"),sQuery(id+"F0.wireOp",EDGE,"g1qmjocW-W1Zj-qumx-oVy1-i4uE7b4poIJz"),sQuery(id+"F0.wireOp",EDGE,"rnIrA8B6-fR9H-q7Qi-GBDJ-2aeuHa1Vv7Qm")])],"isStart":false});
            fillet(context, id + "F2", {"entities" : qUnion([Q0]), "radius" : 1 * mm, "tangentPropagation" : true, "allowEdgeOverflow" : false});
        }
        {
            var Q0;
            Q0=makeQuery(id+"F0.imprint","IMPRINT",FACE,{"disambiguationData":[TD([[makeQuery(id+"F0.imprint","IMPRINT",EDGE,{"derivedFrom":sQuery(id+"F0.wireOp",EDGE,"E0")}),-1.0]])]});
            var Q1;
            Q1=makeQuery(id+"F0.imprint","IMPRINT",FACE,{"disambiguationData":[TD([[makeQuery(id+"F0.imprint","IMPRINT",EDGE,{"derivedFrom":sQuery(id+"F0.wireOp",EDGE,"E42.bottom")}),1.0]])]});
            var Q2;
            Q2=makeQuery(id+"F0.imprint","IMPRINT",FACE,{"disambiguationData":[TD([[makeQuery(id+"F0.imprint","IMPRINT",EDGE,{"derivedFrom":sQuery(id+"F0.wireOp",EDGE,"E49")}),1.0]])]});
            var Q3;
            Q3=makeQuery(id+"F0.imprint","IMPRINT",FACE,{"disambiguationData":[TD([[makeQuery(id+"F0.imprint","IMPRINT",EDGE,{"derivedFrom":sQuery(id+"F0.wireOp",EDGE,"E59")}),-1.0]])]});
            extrude(context, id + "F3", {"entities" : qUnion([Q0, Q1, Q2, Q3]), "operationType" : NewBodyOperationType.REMOVE, "depth" : 9 * mm, "offsetDistance" : 25 * mm});
        }
    });
